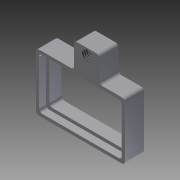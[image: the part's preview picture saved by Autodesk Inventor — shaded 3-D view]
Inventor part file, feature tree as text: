
AUTODESK INVENTOR PART (.ipt)
format: ipt  version: 2011 (Build 150239000, 239)  size: 156,160 bytes
history: native  units: in
note: dims shown in document units (in); Inventor stores cm internally (conversion verified against a paired STEP export)
features: sketch x6, extrude x5, hole x1, thread x1, fillet x1
ambient origin geometry x8: Origin, YZ Plane, XZ Plane, XY Plane, X Axis, Y Axis, Z Axis, Center Point
bodies: Solid1 (feature_tree)
feature tree (14):
  extrude  "Extrusion1"  Depth=0.3543in
  extrude  "Extrusion2"  Depth=0.4724in
  extrude  "Extrusion3"  Depth=0.1181in TaperAngle=0.0deg
  extrude  "Extrusion4"  Depth=0.2362in
  hole  "Hole1"  [1 undecoded]
  thread  "Thread1"  [1 undecoded]
  extrude  "Extrusion5"  Depth=1.0in TaperAngle=0.0deg
  fillet  "Fillet1"  Radius=0.0787in
  sketch  "Sketch1"  dims[d0=0.5512in d1=0.3543in]
  sketch  "Sketch2"  dims[d2=0.1181in d3=0.0in d4=0.4724in]
  sketch  "Sketch3"  dims[d5=0.2756in d6=0.1181in d7=0.0in]
  sketch  "Sketch5"  dims[d13=0.1575in d14=0.2362in]
  sketch  "Sketch6"  dims[d15=0.1575in d16=0.0in d17=0.0197in d18=0.0433in d19=0.0in]
  sketch  "Sketch7"  dims[d20=0.06in d21=0.75in d22=0.375in d23=0.25in d24=0.5635in d25=0.07in d26=0.8108in d27=1.0in d28=0.0in d29=0.0787in d30=0.0394in d31=0.2756in d32=0.0394in d33=0.0in d34=0.0197in]
note: 2 required parameter values undecoded (feature->parameter linkage not recoverable at this tier; creation-order binding heuristic only, values carry confidence <= 0.55)
